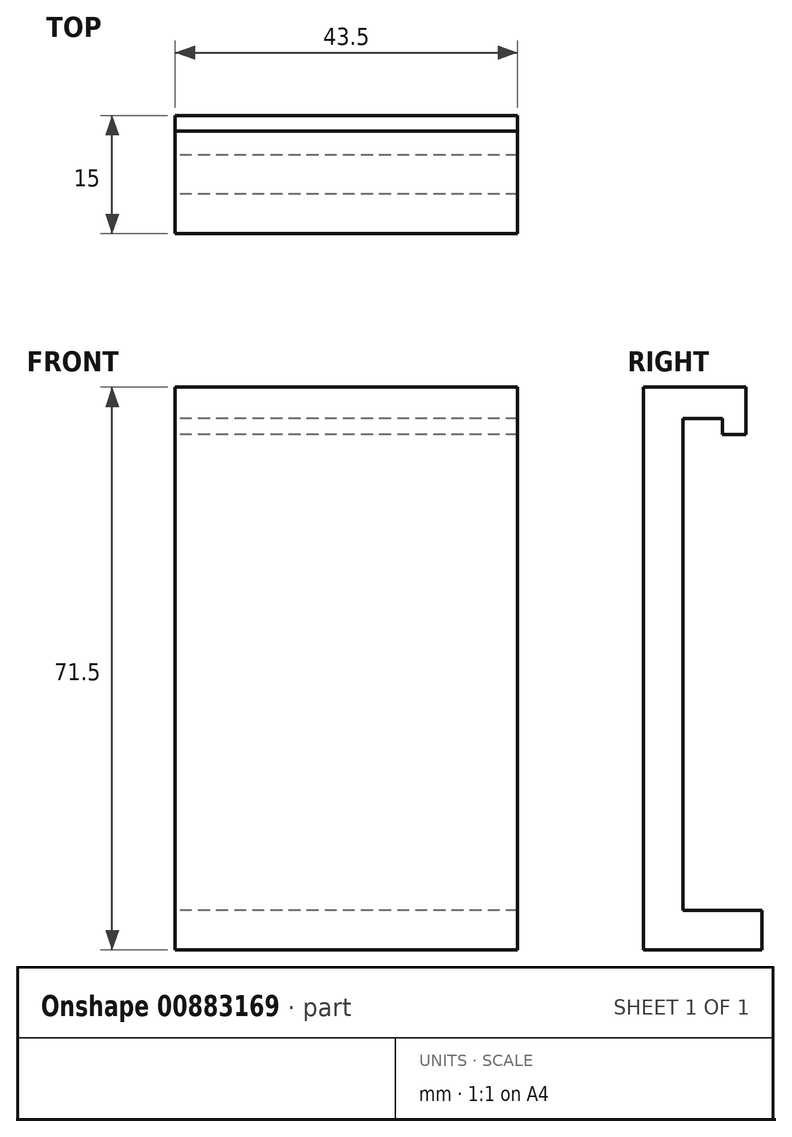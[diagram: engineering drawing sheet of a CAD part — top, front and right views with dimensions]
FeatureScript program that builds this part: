
annotation { "Feature Type Name" : "Feature", "Feature Type Description" : "" }
export const myFeature = defineFeature(function(context is Context, id is Id, definition is map)
    precondition{}
    {
        {
            var Q0;
            Q0=qCreatedBy(makeId("Right.planeOp"),FACE);
            var sketch = newSketch(context, id + "F0", { "sketchPlane" : qUnion([Q0])});
            skLineSegment(sketch, "E0", {"start": v(0, 0) * mm, "end": v(0, -62.5) * mm});
            skLineSegment(sketch, "E1", {"start": v(-5, -67.5) * mm, "end": v(-5, 4) * mm});
            skLineSegment(sketch, "E2", {"start": v(-5, 4) * mm, "end": v(8, 4) * mm});
            skLineSegment(sketch, "E3", {"start": v(8, 4) * mm, "end": v(8, -2) * mm});
            skLineSegment(sketch, "E4", {"start": v(8, -2) * mm, "end": v(5, -2) * mm});
            skLineSegment(sketch, "E5", {"start": v(5, -2) * mm, "end": v(5, 0) * mm});
            skLineSegment(sketch, "E6", {"start": v(5, 0) * mm, "end": v(0, 0) * mm});
            skLineSegment(sketch, "E7", {"start": v(0, -62.5) * mm, "end": v(10, -62.5) * mm});
            skLineSegment(sketch, "E8", {"start": v(10, -62.5) * mm, "end": v(10, -67.5) * mm});
            skLineSegment(sketch, "E9", {"start": v(10, -67.5) * mm, "end": v(-5, -67.5) * mm});
            skSolve(sketch);
        }
        {
            var Q0;
            Q0 = qSketchRegion(id + "F0", true);
            extrude(context, id + "F1", {"entities" : qUnion([Q0]), "depth" : 33.5 * mm, "offsetDistance" : 25 * mm, "hasSecondDirection" : true, "secondDirectionOppositeDirection" : true, "secondDirectionDepth" : 10 * mm});
        }
    });
